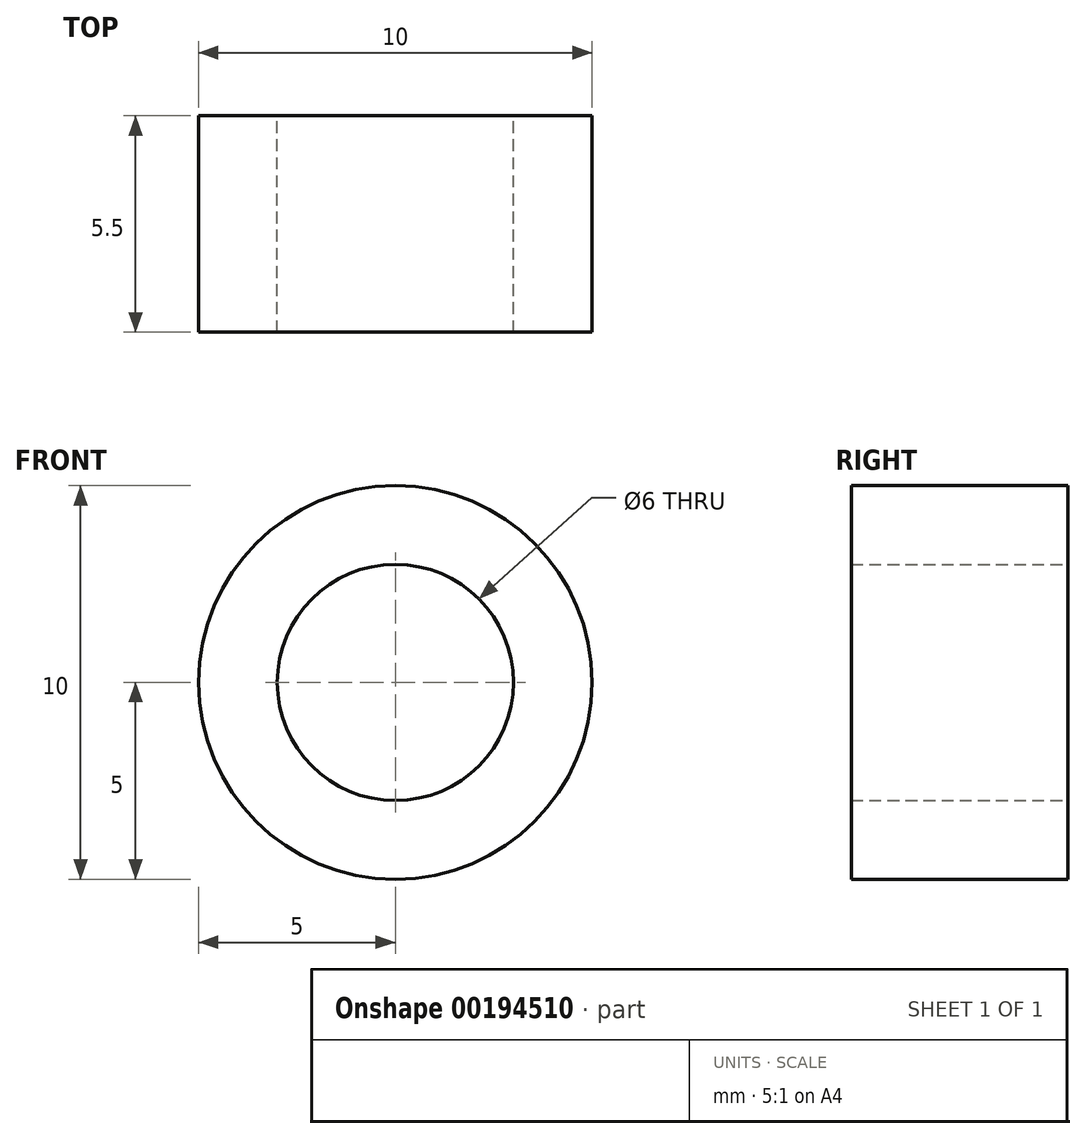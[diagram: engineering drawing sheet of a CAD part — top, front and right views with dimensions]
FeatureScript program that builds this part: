
annotation { "Feature Type Name" : "Feature", "Feature Type Description" : "" }
export const myFeature = defineFeature(function(context is Context, id is Id, definition is map)
    precondition{}
    {
        {
            var Q0;
            Q0=qCreatedBy(makeId("Front.planeOp"),FACE);
            var sketch = newSketch(context, id + "F0", { "sketchPlane" : qUnion([Q0])});
            skCircle(sketch, "E0", {"center": v(0, 0) * mm, "radius": 3 * mm});
            skCircle(sketch, "E1", {"center": v(0, 0) * mm, "radius": 5 * mm});
            skSolve(sketch);
        }
        {
            var Q0;
            Q0 = qSketchRegion(id + "F0", true);
            var Q1;
            Q1=makeQuery(id+"F0.imprint","IMPRINT",FACE,{"disambiguationData":[TD([[makeQuery(id+"F0.imprint","IMPRINT",EDGE,{"derivedFrom":sQuery(id+"F0.wireOp",EDGE,"E0")}),-1.0]])]});
            extrude(context, id + "F1", {"entities" : qUnion([Q0, Q1]), "depth" : 5.5 * mm});
        }
    });
